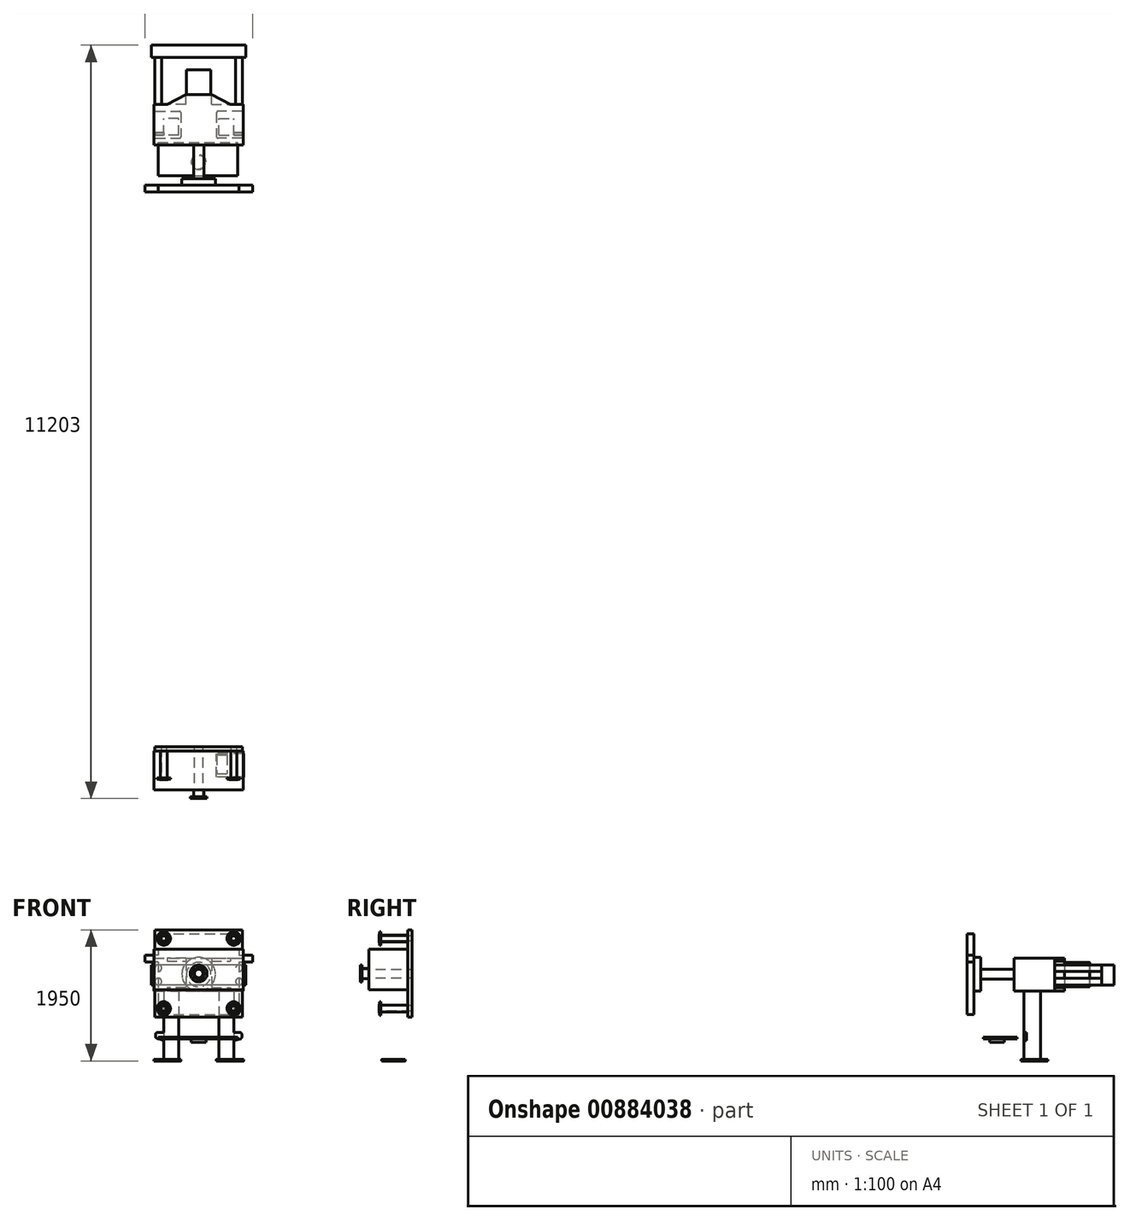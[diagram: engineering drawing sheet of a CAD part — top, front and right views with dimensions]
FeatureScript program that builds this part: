
annotation { "Feature Type Name" : "Feature", "Feature Type Description" : "" }
export const myFeature = defineFeature(function(context is Context, id is Id, definition is map)
    precondition{}
    {
        {
            var Q0;
            Q0=qCreatedBy(makeId("Top.planeOp"),FACE);
            var sketch = newSketch(context, id + "F0", { "sketchPlane" : qUnion([Q0])});
            skLineSegment(sketch, "E0.bottom", {"start": v(-645, 200) * mm, "end": v(-285, 200) * mm});
            skLineSegment(sketch, "E0.top", {"start": v(-645, -200) * mm, "end": v(-285, -200) * mm});
            skLineSegment(sketch, "E0.left", {"start": v(-665, 180) * mm, "end": v(-665, -180) * mm});
            skLineSegment(sketch, "E0.right", {"start": v(-265, 180) * mm, "end": v(-265, -180) * mm});
            skPoint(sketch, "E0.middle", {"position": v(-465, 0) * mm});
            skPoint(sketch, "E1.visualSharp", {"position": v(-665, 200) * mm});
            skArc(sketch, "E1.filletArc", {"start": v(-645, 200) * mm, "mid": v(-659.14, 194.14) * mm, "end": v(-665, 180) * mm});
            skPoint(sketch, "E2.visualSharp", {"position": v(-265, 200) * mm});
            skArc(sketch, "E2.filletArc", {"start": v(-265, 180) * mm, "mid": v(-270.86, 194.14) * mm, "end": v(-285, 200) * mm});
            skPoint(sketch, "E3.visualSharp", {"position": v(-265, -200) * mm});
            skArc(sketch, "E3.filletArc", {"start": v(-285, -200) * mm, "mid": v(-270.86, -194.14) * mm, "end": v(-265, -180) * mm});
            skPoint(sketch, "E4.visualSharp", {"position": v(-665, -200) * mm});
            skArc(sketch, "E4.filletArc", {"start": v(-665, -180) * mm, "mid": v(-659.14, -194.14) * mm, "end": v(-645, -200) * mm});
            skArc(sketch, "E5.MirrorCS", {"start": v(265, 180) * mm, "mid": v(270.86, 194.14) * mm, "end": v(285, 200) * mm});
            skArc(sketch, "E6.MirrorCS", {"start": v(285, -200) * mm, "mid": v(270.86, -194.14) * mm, "end": v(265, -180) * mm});
            skArc(sketch, "E7.MirrorCS", {"start": v(645, 200) * mm, "mid": v(659.14, 194.14) * mm, "end": v(665, 180) * mm});
            skArc(sketch, "E8.MirrorCS", {"start": v(665, -180) * mm, "mid": v(659.14, -194.14) * mm, "end": v(645, -200) * mm});
            skPoint(sketch, "E9.MirrorP", {"position": v(665, -200) * mm});
            skLineSegment(sketch, "E10.MirrorCS", {"start": v(265, 180) * mm, "end": v(265, -180) * mm});
            skPoint(sketch, "E11.MirrorP", {"position": v(665, 200) * mm});
            skPoint(sketch, "E12.MirrorP", {"position": v(265, 200) * mm});
            skLineSegment(sketch, "E13.MirrorCS", {"start": v(665, 180) * mm, "end": v(665, -180) * mm});
            skPoint(sketch, "E14.MirrorP", {"position": v(465, 0) * mm});
            skLineSegment(sketch, "E15.MirrorCS", {"start": v(645, -200) * mm, "end": v(285, -200) * mm});
            skLineSegment(sketch, "E16.MirrorCS", {"start": v(645, 200) * mm, "end": v(285, 200) * mm});
            skPoint(sketch, "E17.MirrorP", {"position": v(265, -200) * mm});
            skSolve(sketch);
        }
        {
            var Q0;
            Q0=makeQuery(id+"F0.imprint","IMPRINT",FACE,{"disambiguationData":[TD([[makeQuery(id+"F0.imprint","IMPRINT",EDGE,{"derivedFrom":sQuery(id+"F0.wireOp",EDGE,"E0.bottom")}),-1.0]])]});
            var sketch = newSketch(context, id + "F1", { "sketchPlane" : qUnion([Q0])});
            skPoint(sketch, "E18.0", {"position": v(-465, 0) * mm});
            skLineSegment(sketch, "E19.bottom", {"start": v(-665, -9700) * mm, "end": v(-265, -9700) * mm});
            skLineSegment(sketch, "E19.top", {"start": v(-665, -9350) * mm, "end": v(-265, -9350) * mm});
            skLineSegment(sketch, "E19.left", {"start": v(-670, -9695) * mm, "end": v(-670, -9355) * mm});
            skLineSegment(sketch, "E19.right", {"start": v(-260, -9695) * mm, "end": v(-260, -9355) * mm});
            skPoint(sketch, "E19.middle", {"position": v(-465, -9525) * mm});
            skPoint(sketch, "E20.visualSharp", {"position": v(-670, -9350) * mm});
            skArc(sketch, "E20.filletArc", {"start": v(-665, -9350) * mm, "mid": v(-668.54, -9351.46) * mm, "end": v(-670, -9355) * mm});
            skPoint(sketch, "E21.visualSharp", {"position": v(-670, -9700) * mm});
            skArc(sketch, "E21.filletArc", {"start": v(-670, -9695) * mm, "mid": v(-668.54, -9698.54) * mm, "end": v(-665, -9700) * mm});
            skPoint(sketch, "E22.visualSharp", {"position": v(-260, -9350) * mm});
            skArc(sketch, "E22.filletArc", {"start": v(-260, -9355) * mm, "mid": v(-261.46, -9351.46) * mm, "end": v(-265, -9350) * mm});
            skPoint(sketch, "E23.visualSharp", {"position": v(-260, -9700) * mm});
            skArc(sketch, "E23.filletArc", {"start": v(-265, -9700) * mm, "mid": v(-261.46, -9698.54) * mm, "end": v(-260, -9695) * mm});
            skArc(sketch, "E24.MirrorCS", {"start": v(260, -9355) * mm, "mid": v(261.46, -9351.46) * mm, "end": v(265, -9350) * mm});
            skArc(sketch, "E25.MirrorCS", {"start": v(670, -9695) * mm, "mid": v(668.54, -9698.54) * mm, "end": v(665, -9700) * mm});
            skArc(sketch, "E26.MirrorCS", {"start": v(265, -9700) * mm, "mid": v(261.46, -9698.54) * mm, "end": v(260, -9695) * mm});
            skArc(sketch, "E27.MirrorCS", {"start": v(665, -9350) * mm, "mid": v(668.54, -9351.46) * mm, "end": v(670, -9355) * mm});
            skLineSegment(sketch, "E28.MirrorCS", {"start": v(670, -9695) * mm, "end": v(670, -9355) * mm});
            skLineSegment(sketch, "E29.MirrorCS", {"start": v(260, -9695) * mm, "end": v(260, -9355) * mm});
            skLineSegment(sketch, "E30.MirrorCS", {"start": v(665, -9350) * mm, "end": v(265, -9350) * mm});
            skLineSegment(sketch, "E31.MirrorCS", {"start": v(665, -9700) * mm, "end": v(265, -9700) * mm});
            skPoint(sketch, "E32.MirrorP", {"position": v(670, -9350) * mm});
            skPoint(sketch, "E33.MirrorP", {"position": v(670, -9700) * mm});
            skPoint(sketch, "E34.MirrorP", {"position": v(260, -9700) * mm});
            skPoint(sketch, "E35.MirrorP", {"position": v(260, -9350) * mm});
            skPoint(sketch, "E36.MirrorP", {"position": v(465, -9525) * mm});
            skSolve(sketch);
        }
        {
            var Q0;
            Q0=qSketchRegion(id+"F0",true);
            var Q1;
            Q1=qSketchRegion(id+"F1",true);
            extrude(context, id + "F2", {"entities" : qUnion([Q0, Q1]), "depth" : 20 * mm, "offsetDistance" : 25 * mm});
        }
        {
            var Q0;
            Q0=makeQuery(id+"F2.opExtrude","CAP_FACE",FACE,{"disambiguationData":[OSD([sQuery(id+"F0.wireOp",EDGE,"E0.bottom"),sQuery(id+"F0.wireOp",EDGE,"E0.top"),sQuery(id+"F0.wireOp",EDGE,"E0.left"),sQuery(id+"F0.wireOp",EDGE,"E0.right"),sQuery(id+"F0.wireOp",EDGE,"E1.filletArc"),sQuery(id+"F0.wireOp",EDGE,"E2.filletArc"),sQuery(id+"F0.wireOp",EDGE,"E3.filletArc"),sQuery(id+"F0.wireOp",EDGE,"E4.filletArc")])],"isStart":false});
            var sketch = newSketch(context, id + "F3", { "sketchPlane" : qUnion([Q0])});
            skLineSegment(sketch, "E37.bottom", {"start": v(-300, -156.09) * mm, "end": v(-520, -156.09) * mm});
            skLineSegment(sketch, "E37.top", {"start": v(-300, 93.91) * mm, "end": v(-520, 93.91) * mm});
            skLineSegment(sketch, "E37.left", {"start": v(-300, -156.09) * mm, "end": v(-300, 93.91) * mm});
            skLineSegment(sketch, "E37.right", {"start": v(-520, -156.09) * mm, "end": v(-520, 93.91) * mm});
            skPoint(sketch, "E37.middle", {"position": v(-410, -31.09) * mm});
            skLineSegment(sketch, "E38.MirrorCS", {"start": v(300, -156.09) * mm, "end": v(520, -156.09) * mm});
            skLineSegment(sketch, "E39.MirrorCS", {"start": v(300, 93.91) * mm, "end": v(520, 93.91) * mm});
            skLineSegment(sketch, "E40.MirrorCS", {"start": v(520, -156.09) * mm, "end": v(520, 93.91) * mm});
            skLineSegment(sketch, "E41.MirrorCS", {"start": v(300, -156.09) * mm, "end": v(300, 93.91) * mm});
            skPoint(sketch, "E42.MirrorP", {"position": v(410, -31.09) * mm});
            skSolve(sketch);
        }
        {
            var Q0;
            Q0=qSketchRegion(id+"F3",true);
            extrude(context, id + "F4", {"entities" : qUnion([Q0]), "operationType" : NewBodyOperationType.ADD, "depth" : 1020 * mm, "offsetDistance" : 25 * mm});
        }
        {
            var Q0;
            Q0=makeQuery(id+"F2.opExtrude","CAP_FACE",FACE,{"disambiguationData":[OSD([sQuery(id+"F1.wireOp",EDGE,"E19.bottom"),sQuery(id+"F1.wireOp",EDGE,"E19.top"),sQuery(id+"F1.wireOp",EDGE,"E19.left"),sQuery(id+"F1.wireOp",EDGE,"E19.right"),sQuery(id+"F1.wireOp",EDGE,"E20.filletArc"),sQuery(id+"F1.wireOp",EDGE,"E21.filletArc"),sQuery(id+"F1.wireOp",EDGE,"E22.filletArc"),sQuery(id+"F1.wireOp",EDGE,"E23.filletArc")])],"isStart":false});
            var sketch = newSketch(context, id + "F5", { "sketchPlane" : qUnion([Q0])});
            skLineSegment(sketch, "E43.bottom", {"start": v(-270, -9370) * mm, "end": v(-420, -9370) * mm});
            skLineSegment(sketch, "E43.top", {"start": v(-270, -9650) * mm, "end": v(-420, -9650) * mm});
            skLineSegment(sketch, "E43.left", {"start": v(-270, -9370) * mm, "end": v(-270, -9650) * mm});
            skLineSegment(sketch, "E43.right", {"start": v(-420, -9370) * mm, "end": v(-420, -9650) * mm});
            skLineSegment(sketch, "E44.MirrorCS", {"start": v(270, -9370) * mm, "end": v(420, -9370) * mm});
            skLineSegment(sketch, "E45.MirrorCS", {"start": v(420, -9370) * mm, "end": v(420, -9650) * mm});
            skLineSegment(sketch, "E46.MirrorCS", {"start": v(270, -9650) * mm, "end": v(420, -9650) * mm});
            skLineSegment(sketch, "E47.MirrorCS", {"start": v(270, -9370) * mm, "end": v(270, -9650) * mm});
            skSolve(sketch);
        }
        {
            var Q0;
            Q0=qSketchRegion(id+"F5",true);
            extrude(context, id + "F6", {"entities" : qUnion([Q0]), "operationType" : NewBodyOperationType.ADD, "depth" : 1040 * mm, "offsetDistance" : 25 * mm});
        }
        {
            var Q0;
            Q0=makeQuery(id+"F4.opExtrude","CAP_FACE",FACE,{"disambiguationData":[OSD([sQuery(id+"F3.wireOp",EDGE,"E37.bottom"),sQuery(id+"F3.wireOp",EDGE,"E37.top"),sQuery(id+"F3.wireOp",EDGE,"E37.left"),sQuery(id+"F3.wireOp",EDGE,"E37.right")])],"isStart":false});
            var sketch = newSketch(context, id + "F7", { "sketchPlane" : qUnion([Q0])});
            skLineSegment(sketch, "E48.bottom", {"start": v(-663.5, 300) * mm, "end": v(-470, 300) * mm});
            skLineSegment(sketch, "E48.top", {"start": v(-663.5, -300) * mm, "end": v(663.5, -300) * mm});
            skLineSegment(sketch, "E48.left", {"start": v(-663.5, 300) * mm, "end": v(-663.5, -300) * mm});
            skLineSegment(sketch, "E48.right", {"start": v(663.5, 300) * mm, "end": v(663.5, -300) * mm});
            skLineSegment(sketch, "E49", {"start": v(-190, 450) * mm, "end": v(190, 450) * mm});
            skLineSegment(sketch, "E50", {"start": v(-190, 450) * mm, "end": v(-470, 300) * mm});
            skLineSegment(sketch, "E51", {"start": v(190, 450) * mm, "end": v(470, 300) * mm});
            skLineSegment(sketch, "E52.trimOffspring", {"start": v(470, 300) * mm, "end": v(663.5, 300) * mm});
            skSolve(sketch);
        }
        {
            var Q0;
            Q0=makeQuery(id+"F7.imprint","IMPRINT",FACE,{"disambiguationData":[TD([[makeQuery(id+"F7.imprint","IMPRINT",EDGE,{"derivedFrom":sQuery(id+"F7.wireOp",EDGE,"E48.bottom")}),-1.0]])]});
            var Q1;
            Q1=makeQuery(id+"F7.imprint","IMPRINT",FACE,{"disambiguationData":[TD([[makeQuery(id+"F7.imprint","IMPRINT",EDGE,{"derivedFrom":makeQuery(id+"F4.opExtrude","CAP_EDGE",EDGE,{"disambiguationData":[OSD([sQuery(id+"F3.wireOp",EDGE,"E37.bottom")])],"isStart":false})}),-1.0]])]});
            extrude(context, id + "F8", {"entities" : qUnion([Q0, Q1]), "operationType" : NewBodyOperationType.ADD, "depth" : 490 * mm, "offsetDistance" : 25 * mm});
        }
        {
            var Q0;
            Q0=makeQuery(id+"F6.opExtrude","CAP_FACE",FACE,{"disambiguationData":[OSD([sQuery(id+"F5.wireOp",EDGE,"E43.bottom"),sQuery(id+"F5.wireOp",EDGE,"E43.top"),sQuery(id+"F5.wireOp",EDGE,"E43.left"),sQuery(id+"F5.wireOp",EDGE,"E43.right")])],"isStart":false});
            var sketch = newSketch(context, id + "F9", { "sketchPlane" : qUnion([Q0])});
            skLineSegment(sketch, "E53.bottom", {"start": v(-663.5, -9310) * mm, "end": v(663.5, -9310) * mm});
            skLineSegment(sketch, "E53.top", {"start": v(-663.5, -9889) * mm, "end": v(663.5, -9889) * mm});
            skLineSegment(sketch, "E53.left", {"start": v(-663.5, -9310) * mm, "end": v(-663.5, -9889) * mm});
            skLineSegment(sketch, "E53.right", {"start": v(663.5, -9310) * mm, "end": v(663.5, -9889) * mm});
            skSolve(sketch);
        }
        {
            var Q0;
            Q0=makeQuery(id+"F9.imprint","IMPRINT",FACE,{"disambiguationData":[TD([[makeQuery(id+"F9.imprint","IMPRINT",EDGE,{"derivedFrom":sQuery(id+"F9.wireOp",EDGE,"E53.bottom")}),-1.0]])]});
            var Q1;
            Q1=makeQuery(id+"F9.imprint","IMPRINT",FACE,{"disambiguationData":[TD([[makeQuery(id+"F9.imprint","IMPRINT",EDGE,{"derivedFrom":makeQuery(id+"F6.opExtrude","CAP_EDGE",EDGE,{"disambiguationData":[OSD([sQuery(id+"F5.wireOp",EDGE,"E43.bottom")])],"isStart":false})}),1.0]])]});
            extrude(context, id + "F10", {"entities" : qUnion([Q0, Q1]), "operationType" : NewBodyOperationType.ADD, "depth" : 600 * mm, "offsetDistance" : 25 * mm});
        }
        {
            var Q0;
            Q0=makeQuery(id+"F8.opExtrude","SWEPT_FACE",FACE,{"disambiguationData":[OSD([sQuery(id+"F7.wireOp",EDGE,"E49")])]});
            var sketch = newSketch(context, id + "F11", { "sketchPlane" : qUnion([Q0])});
            skCircle(sketch, "E54", {"center": v(0, 1285) * mm, "radius": 182 * mm});
            skSolve(sketch);
        }
        {
            var Q0;
            Q0=makeQuery(id+"F11.imprint","IMPRINT",FACE,{"disambiguationData":[TD([[makeQuery(id+"F11.imprint","IMPRINT",EDGE,{"derivedFrom":sQuery(id+"F11.wireOp",EDGE,"E54")}),1.0]])]});
            extrude(context, id + "F12", {"entities" : qUnion([Q0]), "operationType" : NewBodyOperationType.ADD, "depth" : 370 * mm, "offsetDistance" : 25 * mm});
        }
        {
            var Q0;
            Q0=makeQuery(id+"F8.opExtrude","SWEPT_FACE",FACE,{"disambiguationData":[OSD([sQuery(id+"F7.wireOp",EDGE,"E49")])]});
            var sketch = newSketch(context, id + "F13", { "sketchPlane" : qUnion([Q0])});
            skLineSegment(sketch, "E55.bottom", {"start": v(-190, 1484.67) * mm, "end": v(-470, 1484.67) * mm});
            skLineSegment(sketch, "E55.top", {"start": v(-190, 1087.5) * mm, "end": v(-470, 1087.5) * mm});
            skLineSegment(sketch, "E55.left", {"start": v(-190, 1484.67) * mm, "end": v(-190, 1087.5) * mm});
            skLineSegment(sketch, "E55.right", {"start": v(-470, 1484.67) * mm, "end": v(-470, 1087.5) * mm});
            skLineSegment(sketch, "E56.bottom", {"start": v(190, 1484.67) * mm, "end": v(470, 1484.67) * mm});
            skLineSegment(sketch, "E56.top", {"start": v(190, 1087.5) * mm, "end": v(470, 1087.5) * mm});
            skLineSegment(sketch, "E56.left", {"start": v(190, 1484.67) * mm, "end": v(190, 1087.5) * mm});
            skLineSegment(sketch, "E56.right", {"start": v(470, 1484.67) * mm, "end": v(470, 1087.5) * mm});
            skSolve(sketch);
        }
        {
            var Q0;
            Q0=makeQuery(id+"F13.imprint","IMPRINT",FACE,{"disambiguationData":[TD([[makeQuery(id+"F13.imprint","IMPRINT",EDGE,{"derivedFrom":sQuery(id+"F13.wireOp",EDGE,"E55.bottom")}),1.0]])]});
            var Q1;
            Q1=makeQuery(id+"F13.imprint","IMPRINT",FACE,{"disambiguationData":[TD([[makeQuery(id+"F13.imprint","IMPRINT",EDGE,{"derivedFrom":sQuery(id+"F13.wireOp",EDGE,"E56.bottom")}),-1.0]])]});
            extrude(context, id + "F14", {"entities" : qUnion([Q0, Q1]), "operationType" : NewBodyOperationType.REMOVE, "oppositeDirection" : true, "depth" : 150 * mm, "offsetDistance" : 25 * mm});
        }
        {
            var Q0;
            Q0=makeQuery(id+"F10.opExtrude","SWEPT_FACE",FACE,{"disambiguationData":[OSD([sQuery(id+"F9.wireOp",EDGE,"E53.bottom")])]});
            var sketch = newSketch(context, id + "F15", { "sketchPlane" : qUnion([Q0])});
            skLineSegment(sketch, "E57.bottom", {"start": v(-650, 1950) * mm, "end": v(650, 1950) * mm});
            skLineSegment(sketch, "E57.top", {"start": v(-650, 650) * mm, "end": v(650, 650) * mm});
            skLineSegment(sketch, "E57.left", {"start": v(-650, 1950) * mm, "end": v(-650, 650) * mm});
            skLineSegment(sketch, "E57.right", {"start": v(650, 1950) * mm, "end": v(650, 650) * mm});
            skSolve(sketch);
        }
        {
            var Q0;
            Q0=qSketchRegion(id+"F15",true);
            extrude(context, id + "F16", {"entities" : qUnion([Q0]), "operationType" : NewBodyOperationType.ADD, "depth" : 60 * mm, "offsetDistance" : 25 * mm});
        }
        {
            var Q0;
            Q0=makeQuery(id+"F8.opExtrude","SWEPT_FACE",FACE,{"disambiguationData":[OSD([sQuery(id+"F7.wireOp",EDGE,"E48.top")])]});
            var sketch = newSketch(context, id + "F17", { "sketchPlane" : qUnion([Q0])});
            skCircle(sketch, "E58", {"center": v(0, 1290) * mm, "radius": 75 * mm});
            skSolve(sketch);
        }
        {
            var Q0;
            Q0=makeQuery(id+"F17.imprint","IMPRINT",FACE,{"disambiguationData":[TD([[makeQuery(id+"F17.imprint","IMPRINT",EDGE,{"derivedFrom":sQuery(id+"F17.wireOp",EDGE,"E58")}),1.0]])]});
            extrude(context, id + "F18", {"entities" : qUnion([Q0]), "depth" : 600 * mm, "offsetDistance" : 25 * mm});
        }
        {
            var Q0;
            Q0=makeQuery(id+"F18.opExtrude","CAP_FACE",FACE,{"disambiguationData":[OSD([sQuery(id+"F17.wireOp",EDGE,"E58")])],"isStart":false});
            var sketch = newSketch(context, id + "F19", { "sketchPlane" : qUnion([Q0])});
            skLineSegment(sketch, "E59.bottom", {"start": v(-600, 1890) * mm, "end": v(600, 1890) * mm});
            skLineSegment(sketch, "E59.top", {"start": v(-600, 690) * mm, "end": v(600, 690) * mm});
            skLineSegment(sketch, "E59.left", {"start": v(-600, 1890) * mm, "end": v(-600, 1570) * mm});
            skLineSegment(sketch, "E59.right", {"start": v(600, 1890) * mm, "end": v(600, 1570) * mm});
            skPoint(sketch, "E59.middle", {"position": v(0, 1290) * mm});
            skLineSegment(sketch, "E60.bottom", {"start": v(-600, 1570) * mm, "end": v(-800, 1570) * mm});
            skLineSegment(sketch, "E60.top", {"start": v(-600, 1470) * mm, "end": v(-800, 1470) * mm});
            skLineSegment(sketch, "E60.right", {"start": v(-800, 1570) * mm, "end": v(-800, 1470) * mm});
            skLineSegment(sketch, "E61.bottom", {"start": v(600, 1470) * mm, "end": v(800, 1470) * mm});
            skLineSegment(sketch, "E61.top", {"start": v(600, 1570) * mm, "end": v(800, 1570) * mm});
            skLineSegment(sketch, "E61.right", {"start": v(800, 1470) * mm, "end": v(800, 1570) * mm});
            skLineSegment(sketch, "E62.trimOffspring", {"start": v(-600, 1470) * mm, "end": v(-600, 690) * mm});
            skLineSegment(sketch, "E63.trimOffspring", {"start": v(600, 1470) * mm, "end": v(600, 690) * mm});
            skSolve(sketch);
        }
        {
            var Q0;
            Q0=makeQuery(id+"F19.imprint","IMPRINT",FACE,{"disambiguationData":[TD([[makeQuery(id+"F19.imprint","IMPRINT",EDGE,{"derivedFrom":sQuery(id+"F19.wireOp",EDGE,"E59.bottom")}),-1.0]])]});
            var Q1;
            Q1=makeQuery(id+"F19.imprint","IMPRINT",FACE,{"disambiguationData":[TD([[makeQuery(id+"F19.imprint","IMPRINT",EDGE,{"derivedFrom":makeQuery(id+"F18.opExtrude","CAP_EDGE",EDGE,{"disambiguationData":[OSD([sQuery(id+"F17.wireOp",EDGE,"E58")])],"isStart":false})}),1.0]])]});
            extrude(context, id + "F20", {"entities" : qUnion([Q0, Q1]), "operationType" : NewBodyOperationType.ADD, "depth" : 100 * mm, "offsetDistance" : 25 * mm});
        }
        {
            var Q0;
            Q0=makeQuery(id+"F20.opExtrude","CAP_FACE",FACE,{"disambiguationData":[OSD([sQuery(id+"F19.wireOp",EDGE,"E59.bottom"),sQuery(id+"F19.wireOp",EDGE,"E59.top"),sQuery(id+"F19.wireOp",EDGE,"E59.left"),sQuery(id+"F19.wireOp",EDGE,"E59.right"),sQuery(id+"F19.wireOp",EDGE,"E60.bottom"),sQuery(id+"F19.wireOp",EDGE,"E60.top"),sQuery(id+"F19.wireOp",EDGE,"E60.right"),sQuery(id+"F19.wireOp",EDGE,"E61.bottom"),sQuery(id+"F19.wireOp",EDGE,"E61.top"),sQuery(id+"F19.wireOp",EDGE,"E61.right"),sQuery(id+"F19.wireOp",EDGE,"E62.trimOffspring"),sQuery(id+"F19.wireOp",EDGE,"E63.trimOffspring")])],"isStart":true});
            var sketch = newSketch(context, id + "F21", { "sketchPlane" : qUnion([Q0])});
            skCircle(sketch, "E64", {"center": v(0, 1290) * mm, "radius": 250 * mm});
            skSolve(sketch);
        }
        {
            var Q0;
            Q0=makeQuery(id+"F21.imprint","IMPRINT",FACE,{"disambiguationData":[TD([[makeQuery(id+"F21.imprint","IMPRINT",EDGE,{"derivedFrom":sQuery(id+"F21.wireOp",EDGE,"E64")}),1.0]])]});
            extrude(context, id + "F22", {"entities" : qUnion([Q0]), "operationType" : NewBodyOperationType.ADD, "depth" : 100 * mm, "offsetDistance" : 25 * mm});
        }
        {
            var Q0;
            {var subQ0=sQuery(id+"F15.wireOp",EDGE,"E57.left");var subQ1=sQuery(id+"F15.wireOp",EDGE,"E57.bottom");var subQ3=sQuery(id+"F15.wireOp",EDGE,"E57.right");Q0=makeQuery(id+"F16.boolean.opBoolean","SPLIT",FACE,{"disambiguationData":[TD([makeQuery(id+"F16.opExtrude","SWEPT_FACE",FACE,{"disambiguationData":[OSD([subQ1])]})])],"derivedFrom":makeQuery(id+"F16.opExtrude","CAP_FACE",FACE,{"disambiguationData":[OSD([subQ1,sQuery(id+"F15.wireOp",EDGE,"E57.top"),subQ0,subQ3])],"isStart":true})});}
            var sketch = newSketch(context, id + "F23", { "sketchPlane" : qUnion([Q0])});
            skCircle(sketch, "E65", {"center": v(-520, 1820) * mm, "radius": 40 * mm});
            skCircle(sketch, "E66", {"center": v(520, 1820) * mm, "radius": 40 * mm});
            skSolve(sketch);
        }
        {
            var Q0;
            Q0=qSketchRegion(id+"F23",true);
            extrude(context, id + "F24", {"entities" : qUnion([Q0]), "operationType" : NewBodyOperationType.REMOVE, "oppositeDirection" : true, "depth" : 60 * mm, "offsetDistance" : 25 * mm});
        }
        {
            var Q0;
            {var subQ0=sQuery(id+"F15.wireOp",EDGE,"E57.left");var subQ1=sQuery(id+"F15.wireOp",EDGE,"E57.bottom");var subQ3=sQuery(id+"F15.wireOp",EDGE,"E57.right");Q0=makeQuery(id+"F16.boolean.opBoolean","SPLIT",FACE,{"disambiguationData":[TD([makeQuery(id+"F16.opExtrude","SWEPT_FACE",FACE,{"disambiguationData":[OSD([subQ1])]})])],"derivedFrom":makeQuery(id+"F16.opExtrude","CAP_FACE",FACE,{"disambiguationData":[OSD([subQ1,sQuery(id+"F15.wireOp",EDGE,"E57.top"),subQ0,subQ3])],"isStart":true})});}
            var sketch = newSketch(context, id + "F25", { "sketchPlane" : qUnion([Q0])});
            skCircle(sketch, "E67", {"center": v(-520, 1820) * mm, "radius": 50 * mm});
            skCircle(sketch, "E68", {"center": v(-520, 1820) * mm, "radius": 100 * mm});
            skCircle(sketch, "E69", {"center": v(-440, 1820) * mm, "radius": 9 * mm});
            skCircle(sketch, "E70.1.0", {"center": v(-463.43, 1876.57) * mm, "radius": 9 * mm});
            skCircle(sketch, "E70.2.0", {"center": v(-520, 1900) * mm, "radius": 9 * mm});
            skCircle(sketch, "E70.3.0", {"center": v(-576.57, 1876.57) * mm, "radius": 9 * mm});
            skCircle(sketch, "E70.4.0", {"center": v(-600, 1820) * mm, "radius": 9 * mm});
            skCircle(sketch, "E70.5.0", {"center": v(-576.57, 1763.43) * mm, "radius": 9 * mm});
            skCircle(sketch, "E70.6.0", {"center": v(-520, 1740) * mm, "radius": 9 * mm});
            skCircle(sketch, "E70.7.0", {"center": v(-463.43, 1763.43) * mm, "radius": 9 * mm});
            skSolve(sketch);
        }
        {
            var Q0;
            Q0=makeQuery(id+"F25.imprint","IMPRINT",FACE,{"disambiguationData":[TD([[makeQuery(id+"F25.imprint","IMPRINT",EDGE,{"derivedFrom":sQuery(id+"F25.wireOp",EDGE,"E67")}),1.0]])]});
            extrude(context, id + "F26", {"entities" : qUnion([Q0]), "operationType" : NewBodyOperationType.ADD, "depth" : 420 * mm, "offsetDistance" : 25 * mm});
        }
        {
            var Q0;
            Q0=makeQuery(id+"F26.opExtrude","CAP_FACE",FACE,{"disambiguationData":[OSD([sQuery(id+"F23.wireOp",EDGE,"E65"),sQuery(id+"F25.wireOp",EDGE,"E67")])],"isStart":false});
            var sketch = newSketch(context, id + "F27", { "sketchPlane" : qUnion([Q0])});
            skCircle(sketch, "E71.0", {"center": v(-520, 1900) * mm, "radius": 9 * mm});
            skCircle(sketch, "E71.1", {"center": v(-576.57, 1876.57) * mm, "radius": 9 * mm});
            skCircle(sketch, "E72.0", {"center": v(-463.43, 1763.43) * mm, "radius": 9 * mm});
            skCircle(sketch, "E72.1", {"center": v(-520, 1820) * mm, "radius": 50 * mm});
            skCircle(sketch, "E72.2", {"center": v(-520, 1820) * mm, "radius": 100 * mm});
            skCircle(sketch, "E72.3", {"center": v(-440, 1820) * mm, "radius": 9 * mm});
            skCircle(sketch, "E72.4", {"center": v(-463.43, 1876.57) * mm, "radius": 9 * mm});
            skCircle(sketch, "E72.7", {"center": v(-576.57, 1763.43) * mm, "radius": 9 * mm});
            skCircle(sketch, "E72.8", {"center": v(-520, 1820) * mm, "radius": 50 * mm});
            skCircle(sketch, "E72.9", {"center": v(-520, 1820) * mm, "radius": 40 * mm});
            skLineSegment(sketch, "E72.10", {"start": v(-663.5, 1530) * mm, "end": v(-663.5, 1040) * mm});
            skCircle(sketch, "E73.4", {"center": v(-600, 1820) * mm, "radius": 9 * mm});
            skCircle(sketch, "E73.6", {"center": v(-520, 1740) * mm, "radius": 9 * mm});
            skSolve(sketch);
        }
        {
            var Q0;
            Q0=makeQuery(id+"F27.imprint","IMPRINT",FACE,{"disambiguationData":[TD([[makeQuery(id+"F27.imprint","IMPRINT",EDGE,{"derivedFrom":sQuery(id+"F27.wireOp",EDGE,"E72.4")}),-1.0]])]});
            extrude(context, id + "F28", {"entities" : qUnion([Q0]), "operationType" : NewBodyOperationType.ADD, "oppositeDirection" : true, "depth" : 20 * mm, "offsetDistance" : 25 * mm});
        }
        {
            var Q0;
            Q0=makeQuery(id+"F28.boolean.opBoolean","MERGE",FACE,{"derivedFrom":[makeQuery(id+"F26.opExtrude","CAP_FACE",FACE,{"disambiguationData":[OSD([sQuery(id+"F23.wireOp",EDGE,"E65"),sQuery(id+"F25.wireOp",EDGE,"E67")])],"isStart":false}),makeQuery(id+"F28.opExtrude","CAP_FACE",FACE,{"disambiguationData":[OSD([sQuery(id+"F27.wireOp",EDGE,"E72.4"),sQuery(id+"F27.wireOp",EDGE,"E71.0"),sQuery(id+"F27.wireOp",EDGE,"E71.1"),sQuery(id+"F27.wireOp",EDGE,"E72.0"),sQuery(id+"F27.wireOp",EDGE,"E72.1"),sQuery(id+"F27.wireOp",EDGE,"E72.2"),sQuery(id+"F27.wireOp",EDGE,"E72.3"),sQuery(id+"F27.wireOp",EDGE,"E73.4"),sQuery(id+"F27.wireOp",EDGE,"E72.7"),sQuery(id+"F27.wireOp",EDGE,"E73.6")])],"isStart":true})]});
            var sketch = newSketch(context, id + "F29", { "sketchPlane" : qUnion([Q0])});
            skCircle(sketch, "E74", {"center": v(-520, 1820) * mm, "radius": 65 * mm});
            skSolve(sketch);
        }
        {
            var Q0;
            Q0=makeQuery(id+"F29.imprint","IMPRINT",FACE,{"disambiguationData":[TD([[makeQuery(id+"F29.imprint","IMPRINT",EDGE,{"derivedFrom":sQuery(id+"F29.wireOp",EDGE,"E74")}),1.0]])]});
            extrude(context, id + "F30", {"entities" : qUnion([Q0]), "operationType" : NewBodyOperationType.ADD, "depth" : 5 * mm, "offsetDistance" : 25 * mm});
        }
        {
            var Q0;
            Q0=makeQuery(id+"F25.imprint","IMPRINT",FACE,{"disambiguationData":[TD([[makeQuery(id+"F25.imprint","IMPRINT",EDGE,{"derivedFrom":sQuery(id+"F25.wireOp",EDGE,"E68")}),-1.0]])]});
            var sketch = newSketch(context, id + "F31", { "sketchPlane" : qUnion([Q0])});
            skCircle(sketch, "E75.0", {"center": v(520, 1820) * mm, "radius": 40 * mm});
            skCircle(sketch, "E76", {"center": v(520, 1820) * mm, "radius": 45 * mm});
            skCircle(sketch, "E77", {"center": v(520, 1820) * mm, "radius": 100 * mm});
            skCircle(sketch, "E78", {"center": v(600, 1820) * mm, "radius": 9 * mm});
            skCircle(sketch, "E79.1.0", {"center": v(576.57, 1876.57) * mm, "radius": 9 * mm});
            skCircle(sketch, "E79.2.0", {"center": v(520, 1900) * mm, "radius": 9 * mm});
            skCircle(sketch, "E79.3.0", {"center": v(463.43, 1876.57) * mm, "radius": 9 * mm});
            skCircle(sketch, "E79.4.0", {"center": v(440, 1820) * mm, "radius": 9 * mm});
            skCircle(sketch, "E79.5.0", {"center": v(463.43, 1763.43) * mm, "radius": 9 * mm});
            skCircle(sketch, "E79.6.0", {"center": v(520, 1740) * mm, "radius": 9 * mm});
            skCircle(sketch, "E79.7.0", {"center": v(576.57, 1763.43) * mm, "radius": 9 * mm});
            skSolve(sketch);
        }
        {
            var Q0;
            Q0=makeQuery(id+"F31.imprint","IMPRINT",FACE,{"disambiguationData":[TD([[makeQuery(id+"F31.imprint","IMPRINT",EDGE,{"derivedFrom":sQuery(id+"F31.wireOp",EDGE,"E75.0")}),-1.0]])]});
            extrude(context, id + "F32", {"entities" : qUnion([Q0]), "operationType" : NewBodyOperationType.ADD, "depth" : 420 * mm, "offsetDistance" : 25 * mm});
        }
        {
            var Q0;
            Q0=makeQuery(id+"F32.opExtrude","CAP_FACE",FACE,{"disambiguationData":[OSD([sQuery(id+"F31.wireOp",EDGE,"E75.0"),sQuery(id+"F31.wireOp",EDGE,"E76")])],"isStart":false});
            var sketch = newSketch(context, id + "F33", { "sketchPlane" : qUnion([Q0])});
            skCircle(sketch, "E80.0", {"center": v(520, 1820) * mm, "radius": 40 * mm});
            skCircle(sketch, "E80.1", {"center": v(520, 1820) * mm, "radius": 45 * mm});
            skCircle(sketch, "E80.2", {"center": v(600, 1820) * mm, "radius": 9 * mm});
            skCircle(sketch, "E80.3", {"center": v(576.57, 1763.43) * mm, "radius": 9 * mm});
            skCircle(sketch, "E80.4", {"center": v(520, 1900) * mm, "radius": 9 * mm});
            skCircle(sketch, "E80.5", {"center": v(576.57, 1876.57) * mm, "radius": 9 * mm});
            skCircle(sketch, "E80.6", {"center": v(463.43, 1876.57) * mm, "radius": 9 * mm});
            skCircle(sketch, "E80.7", {"center": v(440, 1820) * mm, "radius": 9 * mm});
            skCircle(sketch, "E80.8", {"center": v(520, 1740) * mm, "radius": 9 * mm});
            skCircle(sketch, "E80.9", {"center": v(463.43, 1763.43) * mm, "radius": 9 * mm});
            skCircle(sketch, "E81.0", {"center": v(520, 1820) * mm, "radius": 100 * mm});
            skSolve(sketch);
        }
        {
            var Q0;
            Q0=qSketchRegion(id+"F33",true);
            var Q1;
            Q1=makeQuery(id+"F33.imprint","IMPRINT",FACE,{"disambiguationData":[TD([[makeQuery(id+"F33.imprint","IMPRINT",EDGE,{"derivedFrom":sQuery(id+"F33.wireOp",EDGE,"E80.0")}),-1.0]])]});
            extrude(context, id + "F34", {"entities" : qUnion([Q0, Q1]), "operationType" : NewBodyOperationType.ADD, "oppositeDirection" : true, "depth" : 20 * mm, "offsetDistance" : 25 * mm});
        }
        {
            var Q0;
            Q0=makeQuery(id+"F34.boolean.opBoolean","MERGE",FACE,{"derivedFrom":[makeQuery(id+"F32.opExtrude","CAP_FACE",FACE,{"disambiguationData":[OSD([sQuery(id+"F31.wireOp",EDGE,"E75.0"),sQuery(id+"F31.wireOp",EDGE,"E76")])],"isStart":false}),makeQuery(id+"F34.opExtrude","CAP_FACE",FACE,{"disambiguationData":[OSD([sQuery(id+"F33.wireOp",EDGE,"E80.0"),sQuery(id+"F33.wireOp",EDGE,"E80.2"),sQuery(id+"F33.wireOp",EDGE,"E80.3"),sQuery(id+"F33.wireOp",EDGE,"E80.4"),sQuery(id+"F33.wireOp",EDGE,"E80.5"),sQuery(id+"F33.wireOp",EDGE,"E80.6"),sQuery(id+"F33.wireOp",EDGE,"E80.7"),sQuery(id+"F33.wireOp",EDGE,"E80.8"),sQuery(id+"F33.wireOp",EDGE,"E80.9"),sQuery(id+"F33.wireOp",EDGE,"E81.0")])],"isStart":true})]});
            var sketch = newSketch(context, id + "F35", { "sketchPlane" : qUnion([Q0])});
            skCircle(sketch, "E82", {"center": v(520, 1820) * mm, "radius": 65 * mm});
            skSolve(sketch);
        }
        {
            var Q0;
            Q0=makeQuery(id+"F35.imprint","IMPRINT",FACE,{"disambiguationData":[TD([[makeQuery(id+"F35.imprint","IMPRINT",EDGE,{"derivedFrom":sQuery(id+"F35.wireOp",EDGE,"E82")}),1.0]])]});
            extrude(context, id + "F36", {"entities" : qUnion([Q0]), "operationType" : NewBodyOperationType.ADD, "depth" : 5 * mm, "offsetDistance" : 25 * mm});
        }
        {
            var Q0;
            {var subQ0=sQuery(id+"F15.wireOp",EDGE,"E57.left");var subQ2=sQuery(id+"F15.wireOp",EDGE,"E57.top");var subQ3=sQuery(id+"F15.wireOp",EDGE,"E57.right");Q0=makeQuery(id+"F16.boolean.opBoolean","SPLIT",FACE,{"disambiguationData":[TD([makeQuery(id+"F16.opExtrude","SWEPT_FACE",FACE,{"disambiguationData":[OSD([subQ2])]})])],"derivedFrom":makeQuery(id+"F16.opExtrude","CAP_FACE",FACE,{"disambiguationData":[OSD([sQuery(id+"F15.wireOp",EDGE,"E57.bottom"),subQ2,subQ0,subQ3])],"isStart":true})});}
            var sketch = newSketch(context, id + "F37", { "sketchPlane" : qUnion([Q0])});
            skPoint(sketch, "E83.0", {"position": v(-520, 1820) * mm});
            skCircle(sketch, "E84", {"center": v(-520, 780) * mm, "radius": 40 * mm});
            skCircle(sketch, "E85", {"center": v(520, 780) * mm, "radius": 40 * mm});
            skSolve(sketch);
        }
        {
            var Q0;
            Q0=qSketchRegion(id+"F37",true);
            extrude(context, id + "F38", {"entities" : qUnion([Q0]), "operationType" : NewBodyOperationType.REMOVE, "oppositeDirection" : true, "depth" : 100 * mm, "offsetDistance" : 25 * mm});
        }
        {
            var Q0;
            {var subQ0=sQuery(id+"F15.wireOp",EDGE,"E57.left");var subQ2=sQuery(id+"F15.wireOp",EDGE,"E57.top");var subQ3=sQuery(id+"F15.wireOp",EDGE,"E57.right");Q0=makeQuery(id+"F16.boolean.opBoolean","SPLIT",FACE,{"disambiguationData":[TD([makeQuery(id+"F16.opExtrude","SWEPT_FACE",FACE,{"disambiguationData":[OSD([subQ2])]})])],"derivedFrom":makeQuery(id+"F16.opExtrude","CAP_FACE",FACE,{"disambiguationData":[OSD([sQuery(id+"F15.wireOp",EDGE,"E57.bottom"),subQ2,subQ0,subQ3])],"isStart":true})});}
            var sketch = newSketch(context, id + "F39", { "sketchPlane" : qUnion([Q0])});
            skCircle(sketch, "E86", {"center": v(-520, 780) * mm, "radius": 50 * mm});
            skCircle(sketch, "E87", {"center": v(520, 780) * mm, "radius": 50 * mm});
            skSolve(sketch);
        }
        {
            var Q0;
            Q0=makeQuery(id+"F39.imprint","IMPRINT",FACE,{"disambiguationData":[TD([[makeQuery(id+"F39.imprint","IMPRINT",EDGE,{"derivedFrom":sQuery(id+"F39.wireOp",EDGE,"E86")}),1.0]])]});
            var Q1;
            Q1=makeQuery(id+"F39.imprint","IMPRINT",FACE,{"disambiguationData":[TD([[makeQuery(id+"F39.imprint","IMPRINT",EDGE,{"derivedFrom":sQuery(id+"F39.wireOp",EDGE,"E87")}),1.0]])]});
            extrude(context, id + "F40", {"entities" : qUnion([Q0, Q1]), "operationType" : NewBodyOperationType.ADD, "depth" : 400 * mm, "offsetDistance" : 25 * mm});
        }
        {
            var Q0;
            Q0=makeQuery(id+"F40.opExtrude","CAP_FACE",FACE,{"disambiguationData":[OSD([sQuery(id+"F37.wireOp",EDGE,"E84"),sQuery(id+"F39.wireOp",EDGE,"E86")])],"isStart":false});
            var sketch = newSketch(context, id + "F41", { "sketchPlane" : qUnion([Q0])});
            skCircle(sketch, "E88", {"center": v(-520, 780) * mm, "radius": 100 * mm});
            skCircle(sketch, "E89.0", {"center": v(520, 780) * mm, "radius": 40 * mm});
            skCircle(sketch, "E90", {"center": v(520, 780) * mm, "radius": 100 * mm});
            skCircle(sketch, "E91", {"center": v(-520, 860) * mm, "radius": 9 * mm});
            skCircle(sketch, "E92.1.0", {"center": v(-576.57, 836.57) * mm, "radius": 9 * mm});
            skCircle(sketch, "E92.2.0", {"center": v(-600, 780) * mm, "radius": 9 * mm});
            skCircle(sketch, "E92.3.0", {"center": v(-576.57, 723.43) * mm, "radius": 9 * mm});
            skCircle(sketch, "E92.4.0", {"center": v(-520, 700) * mm, "radius": 9 * mm});
            skCircle(sketch, "E92.5.0", {"center": v(-463.43, 723.43) * mm, "radius": 9 * mm});
            skCircle(sketch, "E92.6.0", {"center": v(-440, 780) * mm, "radius": 9 * mm});
            skCircle(sketch, "E92.7.0", {"center": v(-463.43, 836.57) * mm, "radius": 9 * mm});
            skCircle(sketch, "E93", {"center": v(520, 860) * mm, "radius": 9 * mm});
            skCircle(sketch, "E94.1.0", {"center": v(463.43, 836.57) * mm, "radius": 9 * mm});
            skCircle(sketch, "E94.2.0", {"center": v(440, 780) * mm, "radius": 9 * mm});
            skCircle(sketch, "E94.3.0", {"center": v(463.43, 723.43) * mm, "radius": 9 * mm});
            skCircle(sketch, "E94.4.0", {"center": v(520, 700) * mm, "radius": 9 * mm});
            skCircle(sketch, "E94.5.0", {"center": v(576.57, 723.43) * mm, "radius": 9 * mm});
            skCircle(sketch, "E94.6.0", {"center": v(600, 780) * mm, "radius": 9 * mm});
            skCircle(sketch, "E94.7.0", {"center": v(576.57, 836.57) * mm, "radius": 9 * mm});
            skSolve(sketch);
        }
        {
            var Q0;
            Q0=makeQuery(id+"F41.imprint","IMPRINT",FACE,{"disambiguationData":[TD([[makeQuery(id+"F41.imprint","IMPRINT",EDGE,{"derivedFrom":sQuery(id+"F41.wireOp",EDGE,"E88")}),1.0]])]});
            var Q1;
            Q1=makeQuery(id+"F41.imprint","IMPRINT",FACE,{"disambiguationData":[TD([[makeQuery(id+"F41.imprint","IMPRINT",EDGE,{"derivedFrom":makeQuery(id+"F40.opExtrude","CAP_EDGE",EDGE,{"disambiguationData":[OSD([sQuery(id+"F39.wireOp",EDGE,"E86")])],"isStart":false})}),1.0]])]});
            var Q2;
            Q2=makeQuery(id+"F41.imprint","IMPRINT",FACE,{"disambiguationData":[TD([[makeQuery(id+"F41.imprint","IMPRINT",EDGE,{"derivedFrom":sQuery(id+"F41.wireOp",EDGE,"E89.0")}),-1.0]])]});
            extrude(context, id + "F42", {"entities" : qUnion([Q0, Q1, Q2]), "operationType" : NewBodyOperationType.ADD, "depth" : 20 * mm, "offsetDistance" : 25 * mm});
        }
        {
            var Q0;
            Q0=makeQuery(id+"F42.opExtrude","CAP_FACE",FACE,{"disambiguationData":[OSD([sQuery(id+"F37.wireOp",EDGE,"E84"),sQuery(id+"F41.wireOp",EDGE,"E88"),sQuery(id+"F41.wireOp",EDGE,"E91"),sQuery(id+"F41.wireOp",EDGE,"E92.1.0"),sQuery(id+"F41.wireOp",EDGE,"E92.2.0"),sQuery(id+"F41.wireOp",EDGE,"E92.3.0"),sQuery(id+"F41.wireOp",EDGE,"E92.4.0"),sQuery(id+"F41.wireOp",EDGE,"E92.5.0"),sQuery(id+"F41.wireOp",EDGE,"E92.6.0"),sQuery(id+"F41.wireOp",EDGE,"E92.7.0")])],"isStart":false});
            var sketch = newSketch(context, id + "F43", { "sketchPlane" : qUnion([Q0])});
            skCircle(sketch, "E95", {"center": v(-520, 780) * mm, "radius": 65 * mm});
            skCircle(sketch, "E96.0", {"center": v(520, 780) * mm, "radius": 40 * mm});
            skCircle(sketch, "E97", {"center": v(520, 780) * mm, "radius": 65 * mm});
            skSolve(sketch);
        }
        {
            var Q0;
            Q0=makeQuery(id+"F43.imprint","IMPRINT",FACE,{"disambiguationData":[TD([[makeQuery(id+"F43.imprint","IMPRINT",EDGE,{"derivedFrom":sQuery(id+"F43.wireOp",EDGE,"E95")}),1.0]])]});
            var Q1;
            Q1=makeQuery(id+"F43.imprint","IMPRINT",FACE,{"disambiguationData":[TD([[makeQuery(id+"F43.imprint","IMPRINT",EDGE,{"derivedFrom":sQuery(id+"F43.wireOp",EDGE,"E96.0")}),-1.0]])]});
            extrude(context, id + "F44", {"entities" : qUnion([Q0, Q1]), "operationType" : NewBodyOperationType.ADD, "depth" : 5 * mm, "offsetDistance" : 25 * mm});
        }
        {
            var Q0;
            Q0=makeQuery(id+"F16.opExtrude","CAP_FACE",FACE,{"disambiguationData":[OSD([sQuery(id+"F15.wireOp",EDGE,"E57.bottom"),sQuery(id+"F15.wireOp",EDGE,"E57.top"),sQuery(id+"F15.wireOp",EDGE,"E57.left"),sQuery(id+"F15.wireOp",EDGE,"E57.right")])],"isStart":false});
            var sketch = newSketch(context, id + "F45", { "sketchPlane" : qUnion([Q0])});
            skCircle(sketch, "E98", {"center": v(0, 1300) * mm, "radius": 62.5 * mm});
            skSolve(sketch);
        }
        {
            var Q0;
            Q0=makeQuery(id+"F45.imprint","IMPRINT",FACE,{"disambiguationData":[TD([[makeQuery(id+"F45.imprint","IMPRINT",EDGE,{"derivedFrom":sQuery(id+"F45.wireOp",EDGE,"E98")}),1.0]])]});
            extrude(context, id + "F46", {"entities" : qUnion([Q0]), "operationType" : NewBodyOperationType.REMOVE, "oppositeDirection" : true, "depth" : 800 * mm, "offsetDistance" : 25 * mm});
        }
        {
            var Q0;
            Q0=makeQuery(id+"F10.opExtrude","SWEPT_FACE",FACE,{"disambiguationData":[OSD([sQuery(id+"F9.wireOp",EDGE,"E53.top")])]});
            var sketch = newSketch(context, id + "F47", { "sketchPlane" : qUnion([Q0])});
            skCircle(sketch, "E99", {"center": v(0, 1300) * mm, "radius": 75 * mm});
            skSolve(sketch);
        }
        {
            var Q0;
            Q0=makeQuery(id+"F47.imprint","IMPRINT",FACE,{"disambiguationData":[TD([[makeQuery(id+"F47.imprint","IMPRINT",EDGE,{"derivedFrom":sQuery(id+"F47.wireOp",EDGE,"E99")}),1.0]])]});
            extrude(context, id + "F48", {"entities" : qUnion([Q0]), "operationType" : NewBodyOperationType.ADD, "depth" : 100 * mm, "offsetDistance" : 25 * mm});
        }
        {
            var Q0;
            Q0=makeQuery(id+"F48.opExtrude","CAP_FACE",FACE,{"disambiguationData":[OSD([sQuery(id+"F9.wireOp",EDGE,"E53.top"),sQuery(id+"F45.wireOp",EDGE,"E98"),sQuery(id+"F47.wireOp",EDGE,"E99")])],"isStart":false});
            var sketch = newSketch(context, id + "F49", { "sketchPlane" : qUnion([Q0])});
            skCircle(sketch, "E100", {"center": v(0, 1300) * mm, "radius": 125 * mm});
            skCircle(sketch, "E101", {"center": v(0, 1405) * mm, "radius": 9 * mm});
            skCircle(sketch, "E102.1.0", {"center": v(-74.25, 1374.25) * mm, "radius": 9 * mm});
            skCircle(sketch, "E102.2.0", {"center": v(-105, 1300) * mm, "radius": 9 * mm});
            skCircle(sketch, "E102.3.0", {"center": v(-74.25, 1225.75) * mm, "radius": 9 * mm});
            skCircle(sketch, "E102.4.0", {"center": v(0, 1195) * mm, "radius": 9 * mm});
            skCircle(sketch, "E102.5.0", {"center": v(74.25, 1225.75) * mm, "radius": 9 * mm});
            skCircle(sketch, "E102.6.0", {"center": v(105, 1300) * mm, "radius": 9 * mm});
            skCircle(sketch, "E102.7.0", {"center": v(74.25, 1374.25) * mm, "radius": 9 * mm});
            skSolve(sketch);
        }
        {
            var Q0;
            Q0=makeQuery(id+"F49.imprint","IMPRINT",FACE,{"disambiguationData":[TD([[makeQuery(id+"F49.imprint","IMPRINT",EDGE,{"derivedFrom":sQuery(id+"F49.wireOp",EDGE,"E100")}),1.0]])]});
            var Q1;
            Q1=makeQuery(id+"F49.imprint","IMPRINT",FACE,{"disambiguationData":[TD([[makeQuery(id+"F49.imprint","IMPRINT",EDGE,{"derivedFrom":makeQuery(id+"F48.opExtrude","CAP_EDGE",EDGE,{"disambiguationData":[OSD([sQuery(id+"F47.wireOp",EDGE,"E99")])],"isStart":false})}),1.0]])]});
            extrude(context, id + "F50", {"entities" : qUnion([Q0, Q1]), "operationType" : NewBodyOperationType.ADD, "depth" : 25 * mm, "offsetDistance" : 25 * mm});
        }
        {
            var Q0;
            Q0=makeQuery(id+"F50.opExtrude","CAP_FACE",FACE,{"disambiguationData":[OSD([sQuery(id+"F9.wireOp",EDGE,"E53.top"),sQuery(id+"F45.wireOp",EDGE,"E98"),sQuery(id+"F49.wireOp",EDGE,"E100"),sQuery(id+"F49.wireOp",EDGE,"E101"),sQuery(id+"F49.wireOp",EDGE,"E102.1.0"),sQuery(id+"F49.wireOp",EDGE,"E102.2.0"),sQuery(id+"F49.wireOp",EDGE,"E102.3.0"),sQuery(id+"F49.wireOp",EDGE,"E102.4.0"),sQuery(id+"F49.wireOp",EDGE,"E102.5.0"),sQuery(id+"F49.wireOp",EDGE,"E102.6.0"),sQuery(id+"F49.wireOp",EDGE,"E102.7.0")])],"isStart":false});
            var sketch = newSketch(context, id + "F51", { "sketchPlane" : qUnion([Q0])});
            skCircle(sketch, "E103", {"center": v(0, 1300) * mm, "radius": 85 * mm});
            skSolve(sketch);
        }
        {
            var Q0;
            Q0=makeQuery(id+"F51.imprint","IMPRINT",FACE,{"disambiguationData":[TD([[makeQuery(id+"F51.imprint","IMPRINT",EDGE,{"derivedFrom":sQuery(id+"F51.wireOp",EDGE,"E103")}),1.0]])]});
            extrude(context, id + "F52", {"entities" : qUnion([Q0]), "operationType" : NewBodyOperationType.ADD, "depth" : 5 * mm, "offsetDistance" : 25 * mm});
        }
        {
            var Q0;
            Q0=makeQuery(id+"F14.boolean.opBoolean","MERGE",FACE,{"derivedFrom":[makeQuery(id+"F8.opExtrude","SWEPT_FACE",FACE,{"disambiguationData":[OSD([sQuery(id+"F7.wireOp",EDGE,"E52.trimOffspring")])]}),makeQuery(id+"F14.opExtrude","CAP_FACE",FACE,{"disambiguationData":[OSD([sQuery(id+"F13.wireOp",EDGE,"E55.bottom"),sQuery(id+"F13.wireOp",EDGE,"E55.top"),sQuery(id+"F13.wireOp",EDGE,"E55.left"),sQuery(id+"F13.wireOp",EDGE,"E55.right")])],"isStart":false})]});
            var sketch = newSketch(context, id + "F53", { "sketchPlane" : qUnion([Q0])});
            skCircle(sketch, "E104", {"center": v(-600, 1379.34) * mm, "radius": 50 * mm});
            skCircle(sketch, "E105", {"center": v(-600, 1179.34) * mm, "radius": 50 * mm});
            skCircle(sketch, "E106.MirrorC", {"center": v(600, 1379.34) * mm, "radius": 50 * mm});
            skCircle(sketch, "E107.MirrorC", {"center": v(600, 1179.34) * mm, "radius": 50 * mm});
            skSolve(sketch);
        }
        {
            var Q0;
            Q0=qSketchRegion(id+"F53",true);
            extrude(context, id + "F54", {"entities" : qUnion([Q0]), "operationType" : NewBodyOperationType.ADD, "depth" : 700 * mm, "offsetDistance" : 25 * mm});
        }
        {
            var Q0;
            Q0=makeQuery(id+"F54.opExtrude","CAP_FACE",FACE,{"disambiguationData":[OSD([sQuery(id+"F53.wireOp",EDGE,"E104")])],"isStart":false});
            var sketch = newSketch(context, id + "F55", { "sketchPlane" : qUnion([Q0])});
            skLineSegment(sketch, "E108.bottom", {"start": v(-700, 1429.34) * mm, "end": v(700, 1429.34) * mm});
            skLineSegment(sketch, "E108.top", {"start": v(-700, 1129.34) * mm, "end": v(700, 1129.34) * mm});
            skLineSegment(sketch, "E108.left", {"start": v(-700, 1429.34) * mm, "end": v(-700, 1129.34) * mm});
            skLineSegment(sketch, "E108.right", {"start": v(700, 1429.34) * mm, "end": v(700, 1129.34) * mm});
            skSolve(sketch);
        }
        {
            var Q0;
            Q0=qSketchRegion(id+"F55",true);
            extrude(context, id + "F56", {"entities" : qUnion([Q0]), "operationType" : NewBodyOperationType.ADD, "depth" : 184 * mm, "offsetDistance" : 25 * mm});
        }
        {
            var Q0;
            Q0=makeQuery(id+"F4.opExtrude","SWEPT_FACE",FACE,{"disambiguationData":[OSD([sQuery(id+"F3.wireOp",EDGE,"E38.MirrorCS")])]});
            var sketch = newSketch(context, id + "F57", { "sketchPlane" : qUnion([Q0])});
            skLineSegment(sketch, "E109", {"start": v(520, 420) * mm, "end": v(620, 420) * mm});
            skLineSegment(sketch, "E110", {"start": v(640, 400) * mm, "end": v(640, 350) * mm});
            skLineSegment(sketch, "E111", {"start": v(625.6, 330.8) * mm, "end": v(520, 300) * mm});
            skPoint(sketch, "E112.visualSharp", {"position": v(640, 420) * mm});
            skArc(sketch, "E112.filletArc", {"start": v(640, 400) * mm, "mid": v(634.14, 414.14) * mm, "end": v(620, 420) * mm});
            skPoint(sketch, "E113.visualSharp", {"position": v(640, 335) * mm});
            skArc(sketch, "E113.filletArc", {"start": v(625.6, 330.8) * mm, "mid": v(636, 338) * mm, "end": v(640, 350) * mm});
            skLineSegment(sketch, "E114.0", {"start": v(-520, 1040) * mm, "end": v(-520, 20) * mm});
            skLineSegment(sketch, "E115", {"start": v(-520, 420) * mm, "end": v(-620, 420) * mm});
            skLineSegment(sketch, "E116", {"start": v(-640, 400) * mm, "end": v(-640, 358.54) * mm});
            skLineSegment(sketch, "E117", {"start": v(-626.97, 339.8) * mm, "end": v(-520, 300) * mm});
            skPoint(sketch, "E118.visualSharp", {"position": v(-640, 420) * mm});
            skArc(sketch, "E118.filletArc", {"start": v(-620, 420) * mm, "mid": v(-634.14, 414.14) * mm, "end": v(-640, 400) * mm});
            skPoint(sketch, "E119.visualSharp", {"position": v(-640, 344.64) * mm});
            skArc(sketch, "E119.filletArc", {"start": v(-640, 358.54) * mm, "mid": v(-636.42, 347.13) * mm, "end": v(-626.97, 339.8) * mm});
            skSolve(sketch);
        }
        {
            var Q0;
            Q0=qSketchRegion(id+"F57",true);
            var Q1;
            {var subQ1=sQuery(id+"F57.wireOp",EDGE,"E109");Q1=makeQuery(id+"F57.imprint","IMPRINT",FACE,{"disambiguationData":[TD([[makeQuery(id+"F57.imprint","IMPRINT",EDGE,{"derivedFrom":subQ1}),-1.0]])]});}
            extrude(context, id + "F58", {"entities" : qUnion([Q0, Q1]), "operationType" : NewBodyOperationType.ADD, "oppositeDirection" : true, "depth" : 40 * mm, "offsetDistance" : 25 * mm});
        }
        {
            var Q0;
            Q0=makeQuery(id+"F58.boolean.opBoolean","MERGE",FACE,{"derivedFrom":[makeQuery(id+"F4.opExtrude","SWEPT_FACE",FACE,{"disambiguationData":[OSD([sQuery(id+"F3.wireOp",EDGE,"E37.bottom")])]}),makeQuery(id+"F58.opExtrude","CAP_FACE",FACE,{"disambiguationData":[OSD([sQuery(id+"F57.wireOp",EDGE,"E114.0"),sQuery(id+"F57.wireOp",EDGE,"E115"),sQuery(id+"F57.wireOp",EDGE,"E116"),sQuery(id+"F57.wireOp",EDGE,"E117"),sQuery(id+"F57.wireOp",EDGE,"E118.filletArc"),sQuery(id+"F57.wireOp",EDGE,"E119.filletArc")])],"isStart":true})]});
            var sketch = newSketch(context, id + "F59", { "sketchPlane" : qUnion([Q0])});
            skLineSegment(sketch, "E120", {"start": v(-596.04, 479.14) * mm, "end": v(-654.32, 239.88) * mm});
            skLineSegment(sketch, "E121", {"start": v(-654.32, 239.88) * mm, "end": v(-538.78, 176.67) * mm});
            skLineSegment(sketch, "E122", {"start": v(-538.78, 176.67) * mm, "end": v(-438.08, 360.72) * mm});
            skLineSegment(sketch, "E123", {"start": v(-438.08, 360.72) * mm, "end": v(-596.04, 479.14) * mm});
            skLineSegment(sketch, "E124", {"start": v(402.57, 479.14) * mm, "end": v(483.87, 479.14) * mm});
            skLineSegment(sketch, "E125", {"start": v(483.87, 479.14) * mm, "end": v(670.96, 300) * mm});
            skLineSegment(sketch, "E126", {"start": v(670.96, 300) * mm, "end": v(613.4, 239.88) * mm});
            skLineSegment(sketch, "E127", {"start": v(613.4, 239.88) * mm, "end": v(425.29, 420) * mm});
            skLineSegment(sketch, "E128", {"start": v(425.29, 420) * mm, "end": v(402.57, 479.14) * mm});
            skSolve(sketch);
        }
        {
            var Q0;
            Q0=makeQuery(id+"F6.opExtrude","SWEPT_FACE",FACE,{"disambiguationData":[OSD([sQuery(id+"F5.wireOp",EDGE,"E44.MirrorCS")])]});
            var sketch = newSketch(context, id + "F60", { "sketchPlane" : qUnion([Q0])});
            skLineSegment(sketch, "E129.bottom", {"start": v(-420, 420) * mm, "end": v(-617.72, 420) * mm});
            skLineSegment(sketch, "E129.top", {"start": v(-420, 345) * mm, "end": v(-617.72, 345) * mm});
            skLineSegment(sketch, "E129.left", {"start": v(-420, 420) * mm, "end": v(-420, 345) * mm});
            skLineSegment(sketch, "E129.right", {"start": v(-637.72, 400) * mm, "end": v(-637.72, 365) * mm});
            skLineSegment(sketch, "E130.bottom", {"start": v(420, 345) * mm, "end": v(620, 345) * mm});
            skLineSegment(sketch, "E130.top", {"start": v(420, 420) * mm, "end": v(620, 420) * mm});
            skLineSegment(sketch, "E130.left", {"start": v(420, 345) * mm, "end": v(420, 420) * mm});
            skLineSegment(sketch, "E130.right", {"start": v(640, 365) * mm, "end": v(640, 400) * mm});
            skPoint(sketch, "E131.visualSharp", {"position": v(640, 420) * mm});
            skArc(sketch, "E131.filletArc", {"start": v(640, 400) * mm, "mid": v(634.14, 414.14) * mm, "end": v(620, 420) * mm});
            skPoint(sketch, "E132.visualSharp", {"position": v(640, 345) * mm});
            skArc(sketch, "E132.filletArc", {"start": v(620, 345) * mm, "mid": v(634.14, 350.86) * mm, "end": v(640, 365) * mm});
            skPoint(sketch, "E133.visualSharp", {"position": v(-637.72, 420) * mm});
            skArc(sketch, "E133.filletArc", {"start": v(-617.72, 420) * mm, "mid": v(-631.86, 414.14) * mm, "end": v(-637.72, 400) * mm});
            skPoint(sketch, "E134.visualSharp", {"position": v(-637.72, 345) * mm});
            skArc(sketch, "E134.filletArc", {"start": v(-637.72, 365) * mm, "mid": v(-631.86, 350.86) * mm, "end": v(-617.72, 345) * mm});
            skSolve(sketch);
        }
        {
            var Q0;
            Q0=makeQuery(id+"F2.opExtrude","CAP_FACE",FACE,{"disambiguationData":[OSD([sQuery(id+"F0.wireOp",EDGE,"E5.MirrorCS"),sQuery(id+"F0.wireOp",EDGE,"E6.MirrorCS"),sQuery(id+"F0.wireOp",EDGE,"E7.MirrorCS"),sQuery(id+"F0.wireOp",EDGE,"E8.MirrorCS"),sQuery(id+"F0.wireOp",EDGE,"E10.MirrorCS"),sQuery(id+"F0.wireOp",EDGE,"E13.MirrorCS"),sQuery(id+"F0.wireOp",EDGE,"E15.MirrorCS"),sQuery(id+"F0.wireOp",EDGE,"E16.MirrorCS")])],"isStart":true});
            cPlane(context, id + "F61", {"entities" : qUnion([Q0]), "cplaneType" : CPlaneType.OFFSET, "offset" : 350 * mm, "oppositeDirection" : true, "width" : 150 * mm, "height" : 150 * mm});
        }
        {
            var Q0;
            Q0=qCreatedBy(id+"F61.planeOp",FACE);
            var sketch = newSketch(context, id + "F62", { "sketchPlane" : qUnion([Q0])});
            skLineSegment(sketch, "E135.bottom", {"start": v(-602.8, 759.48) * mm, "end": v(579.12, 759.48) * mm});
            skLineSegment(sketch, "E135.top", {"start": v(-602.8, 259.48) * mm, "end": v(579.12, 259.48) * mm});
            skLineSegment(sketch, "E135.left", {"start": v(-602.8, 759.48) * mm, "end": v(-602.8, 259.48) * mm});
            skLineSegment(sketch, "E135.right", {"start": v(579.12, 759.48) * mm, "end": v(579.12, 259.48) * mm});
            skSolve(sketch);
        }
        {
            var Q0;
            Q0=qSketchRegion(id+"F62",true);
            extrude(context, id + "F63", {"entities" : qUnion([Q0]), "operationType" : NewBodyOperationType.ADD, "depth" : 25 * mm, "offsetDistance" : 25 * mm});
        }
        {
            var Q0;
            Q0=makeQuery(id+"F63.opExtrude","CAP_FACE",FACE,{"disambiguationData":[OSD([sQuery(id+"F62.wireOp",EDGE,"E135.bottom"),sQuery(id+"F62.wireOp",EDGE,"E135.top"),sQuery(id+"F62.wireOp",EDGE,"E135.left"),sQuery(id+"F62.wireOp",EDGE,"E135.right")])],"isStart":false});
            var sketch = newSketch(context, id + "F64", { "sketchPlane" : qUnion([Q0])});
            skCircle(sketch, "E136", {"center": v(0, 556.09) * mm, "radius": 100 * mm});
            skCircle(sketch, "E137", {"center": v(0, 556.09) * mm, "radius": 110 * mm});
            skLineSegment(sketch, "E138.0.0", {"start": v(543.46, 156.09) * mm, "end": v(613.4, 156.09) * mm});
            skLineSegment(sketch, "E138.0.1", {"start": v(613.4, 156.09) * mm, "end": v(613.4, 9356.09) * mm});
            skLineSegment(sketch, "E138.0.2", {"start": v(613.4, 9356.09) * mm, "end": v(425.29, 9356.09) * mm});
            skLineSegment(sketch, "E138.0.3", {"start": v(425.29, 9356.09) * mm, "end": v(425.29, 156.09) * mm});
            skLineSegment(sketch, "E138.0.4", {"start": v(425.29, 156.09) * mm, "end": v(543.46, 156.09) * mm});
            skSolve(sketch);
        }
        {
            var Q0;
            Q0=makeQuery(id+"F64.imprint","IMPRINT",FACE,{"disambiguationData":[TD([[makeQuery(id+"F64.imprint","IMPRINT",EDGE,{"derivedFrom":sQuery(id+"F64.wireOp",EDGE,"E136")}),-1.0]])]});
            extrude(context, id + "F65", {"entities" : qUnion([Q0]), "operationType" : NewBodyOperationType.ADD, "depth" : 50 * mm, "offsetDistance" : 25 * mm});
        }
        {
            var Q0;
            Q0=makeQuery(id+"F2.opExtrude","CAP_FACE",FACE,{"disambiguationData":[OSD([sQuery(id+"F1.wireOp",EDGE,"E24.MirrorCS"),sQuery(id+"F1.wireOp",EDGE,"E25.MirrorCS"),sQuery(id+"F1.wireOp",EDGE,"E26.MirrorCS"),sQuery(id+"F1.wireOp",EDGE,"E27.MirrorCS"),sQuery(id+"F1.wireOp",EDGE,"E28.MirrorCS"),sQuery(id+"F1.wireOp",EDGE,"E29.MirrorCS"),sQuery(id+"F1.wireOp",EDGE,"E30.MirrorCS"),sQuery(id+"F1.wireOp",EDGE,"E31.MirrorCS")])],"isStart":true});
            var sketch = newSketch(context, id + "F66", { "sketchPlane" : qUnion([Q0])});
            skLineSegment(sketch, "E139.bottom", {"start": v(-689.5, 9716.62) * mm, "end": v(687.91, 9716.62) * mm});
            skLineSegment(sketch, "E139.top", {"start": v(-689.5, 9333.23) * mm, "end": v(687.91, 9333.23) * mm});
            skLineSegment(sketch, "E139.left", {"start": v(-689.5, 9716.62) * mm, "end": v(-689.5, 9333.23) * mm});
            skLineSegment(sketch, "E139.right", {"start": v(687.91, 9716.62) * mm, "end": v(687.91, 9333.23) * mm});
            skSolve(sketch);
        }
        {
            var Q0;
            Q0=makeQuery(id+"F66.imprint","IMPRINT",FACE,{"disambiguationData":[TD([[makeQuery(id+"F66.imprint","IMPRINT",EDGE,{"derivedFrom":sQuery(id+"F66.wireOp",EDGE,"E139.bottom")}),-1.0]])]});
            var Q1;
            Q1=makeQuery(id+"F66.imprint","IMPRINT",FACE,{"disambiguationData":[TD([[makeQuery(id+"F66.imprint","IMPRINT",EDGE,{"derivedFrom":makeQuery(id+"F2.opExtrude","CAP_EDGE",EDGE,{"disambiguationData":[OSD([sQuery(id+"F1.wireOp",EDGE,"E24.MirrorCS")])],"isStart":true})}),1.0]])]});
            extrude(context, id + "F67", {"entities" : qUnion([Q0, Q1]), "operationType" : NewBodyOperationType.REMOVE, "oppositeDirection" : true, "depth" : 25 * mm, "offsetDistance" : 25 * mm});
        }
        {
            var Q0;
            Q0=makeQuery(id+"F67.boolean.opBoolean","COPY",FACE,{"disambiguationData":[TD([makeQuery(id+"F6.opExtrude","SWEPT_FACE",FACE,{"disambiguationData":[OSD([sQuery(id+"F5.wireOp",EDGE,"E43.bottom")])]})])],"derivedFrom":makeQuery(id+"F67.opExtrude","CAP_FACE",FACE,{"disambiguationData":[OSD([sQuery(id+"F66.wireOp",EDGE,"E139.bottom"),sQuery(id+"F66.wireOp",EDGE,"E139.top"),sQuery(id+"F66.wireOp",EDGE,"E139.left"),sQuery(id+"F66.wireOp",EDGE,"E139.right")])],"isStart":false})});
            var sketch = newSketch(context, id + "F68", { "sketchPlane" : qUnion([Q0])});
            skLineSegment(sketch, "E140.0.0", {"start": v(-420, 9650) * mm, "end": v(-420, 9370) * mm});
            skLineSegment(sketch, "E140.0.1", {"start": v(-420, 9370) * mm, "end": v(-270, 9370) * mm});
            skLineSegment(sketch, "E140.0.2", {"start": v(-270, 9370) * mm, "end": v(-270, 9650) * mm});
            skLineSegment(sketch, "E140.0.3", {"start": v(-270, 9650) * mm, "end": v(-420, 9650) * mm});
            skLineSegment(sketch, "E141.0.0", {"start": v(420, 9370) * mm, "end": v(420, 9650) * mm});
            skLineSegment(sketch, "E141.0.1", {"start": v(420, 9650) * mm, "end": v(270, 9650) * mm});
            skLineSegment(sketch, "E141.0.2", {"start": v(270, 9650) * mm, "end": v(270, 9370) * mm});
            skLineSegment(sketch, "E141.0.3", {"start": v(270, 9370) * mm, "end": v(420, 9370) * mm});
            skSolve(sketch);
        }
        {
            var Q0;
            Q0 = qSketchRegion(id + "F68", true);
            extrude(context, id + "F69", {"entities" : qUnion([Q0]), "operationType" : NewBodyOperationType.REMOVE, "oppositeDirection" : true, "depth" : 1035 * mm, "offsetDistance" : 25 * mm});
        }
    });
